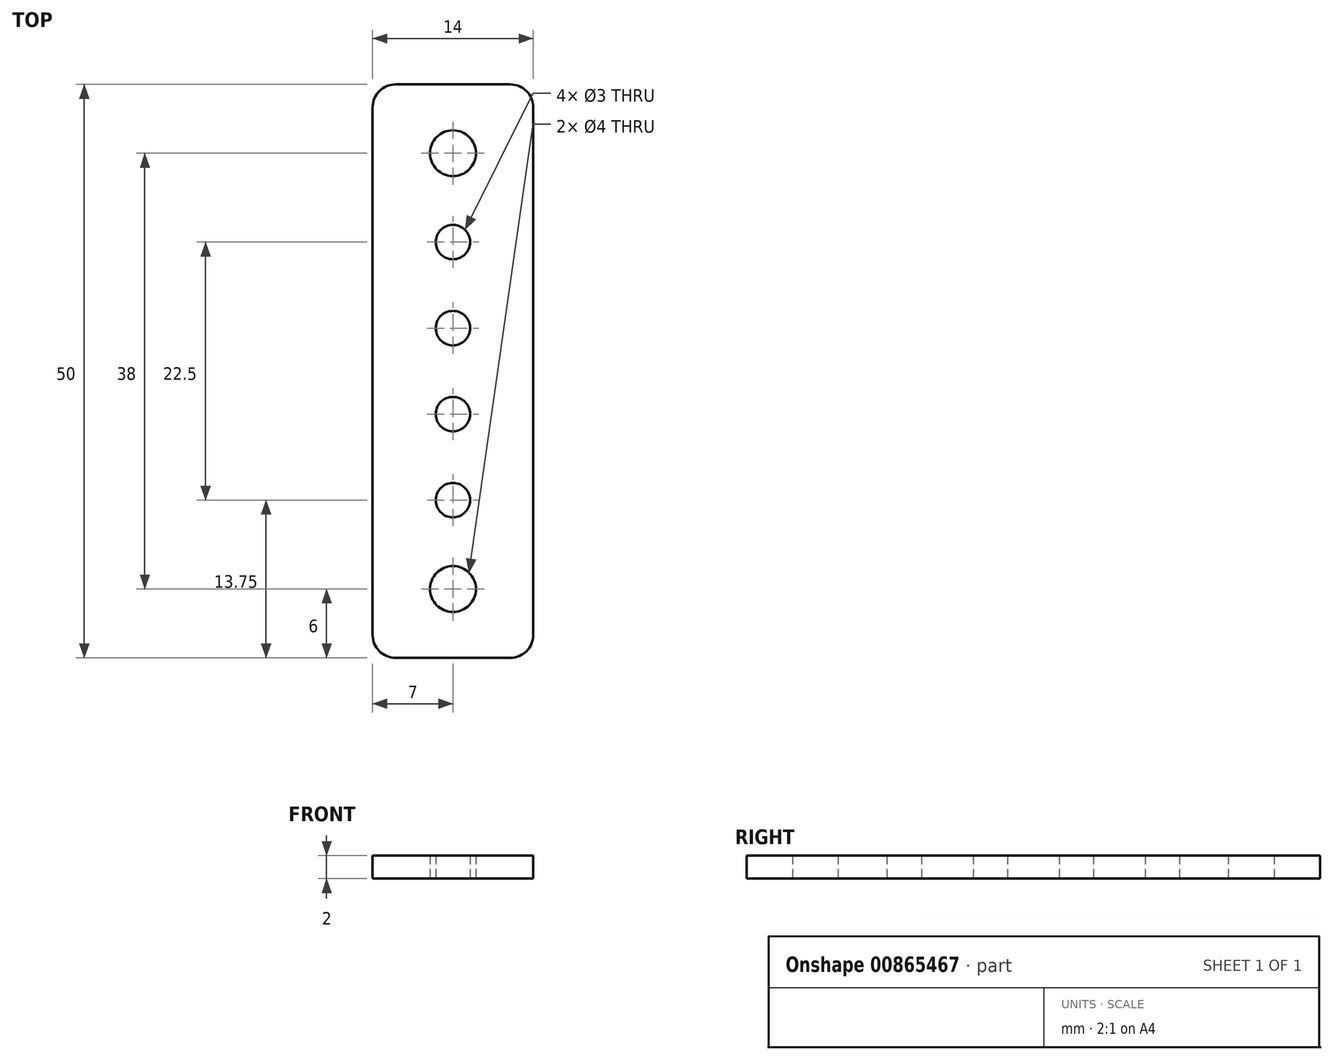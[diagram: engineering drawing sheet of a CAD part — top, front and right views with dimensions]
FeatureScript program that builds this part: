
annotation { "Feature Type Name" : "Feature", "Feature Type Description" : "" }
export const myFeature = defineFeature(function(context is Context, id is Id, definition is map)
    precondition{}
    {
        {
            var Q0;
            Q0=qCreatedBy(makeId("Top.planeOp"),FACE);
            var sketch = newSketch(context, id + "F0", { "sketchPlane" : qUnion([Q0])});
            skLineSegment(sketch, "E0.bottom", {"start": v(5, 25) * mm, "end": v(-5, 25) * mm});
            skLineSegment(sketch, "E0.top", {"start": v(5, -25) * mm, "end": v(-5, -25) * mm});
            skLineSegment(sketch, "E0.left", {"start": v(7, 23) * mm, "end": v(7, -23) * mm});
            skLineSegment(sketch, "E0.right", {"start": v(-7, 23) * mm, "end": v(-7, -23) * mm});
            skPoint(sketch, "E0.middle", {"position": v(0, 0) * mm});
            skPoint(sketch, "E1.visualSharp", {"position": v(-7, 25) * mm});
            skArc(sketch, "E1.filletArc", {"start": v(-5, 25) * mm, "mid": v(-6.41, 24.41) * mm, "end": v(-7, 23) * mm});
            skPoint(sketch, "E2.visualSharp", {"position": v(-7, -25) * mm});
            skArc(sketch, "E2.filletArc", {"start": v(-7, -23) * mm, "mid": v(-6.41, -24.41) * mm, "end": v(-5, -25) * mm});
            skPoint(sketch, "E3.visualSharp", {"position": v(7, -25) * mm});
            skArc(sketch, "E3.filletArc", {"start": v(5, -25) * mm, "mid": v(6.41, -24.41) * mm, "end": v(7, -23) * mm});
            skPoint(sketch, "E4.visualSharp", {"position": v(7, 25) * mm});
            skArc(sketch, "E4.filletArc", {"start": v(7, 23) * mm, "mid": v(6.41, 24.41) * mm, "end": v(5, 25) * mm});
            skPoint(sketch, "E5.center.orphan", {"position": v(-5.5, 0) * mm});
            skPoint(sketch, "E6.center.orphan", {"position": v(5.5, 0) * mm});
            skCircle(sketch, "E7", {"center": v(0, 19) * mm, "radius": 2 * mm});
            skCircle(sketch, "E8", {"center": v(0, -19) * mm, "radius": 2 * mm});
            skPoint(sketch, "E8.centerSnap0", {"position": v(0, 25) * mm});
            skCircle(sketch, "E9", {"center": v(0, 11.25) * mm, "radius": 1.5 * mm});
            skCircle(sketch, "E10.0.1.0", {"center": v(0, 3.75) * mm, "radius": 1.5 * mm});
            skCircle(sketch, "E10.0.2.0", {"center": v(0, -3.75) * mm, "radius": 1.5 * mm});
            skCircle(sketch, "E10.0.3.0", {"center": v(0, -11.25) * mm, "radius": 1.5 * mm});
            skLineSegment(sketch, "E10.direction1", {"start": v(0, 11.25) * mm, "end": v(25, 11.25) * mm, "construction": true});
            skLineSegment(sketch, "E10.direction2", {"start": v(0, 11.25) * mm, "end": v(0, 3.75) * mm, "construction": true});
            skSolve(sketch);
        }
        {
            var Q0;
            Q0=qSketchRegion(id+"F0",true);
            extrude(context, id + "F1", {"entities" : qUnion([Q0]), "depth" : 2 * mm, "offsetDistance" : 25 * mm});
        }
    });
